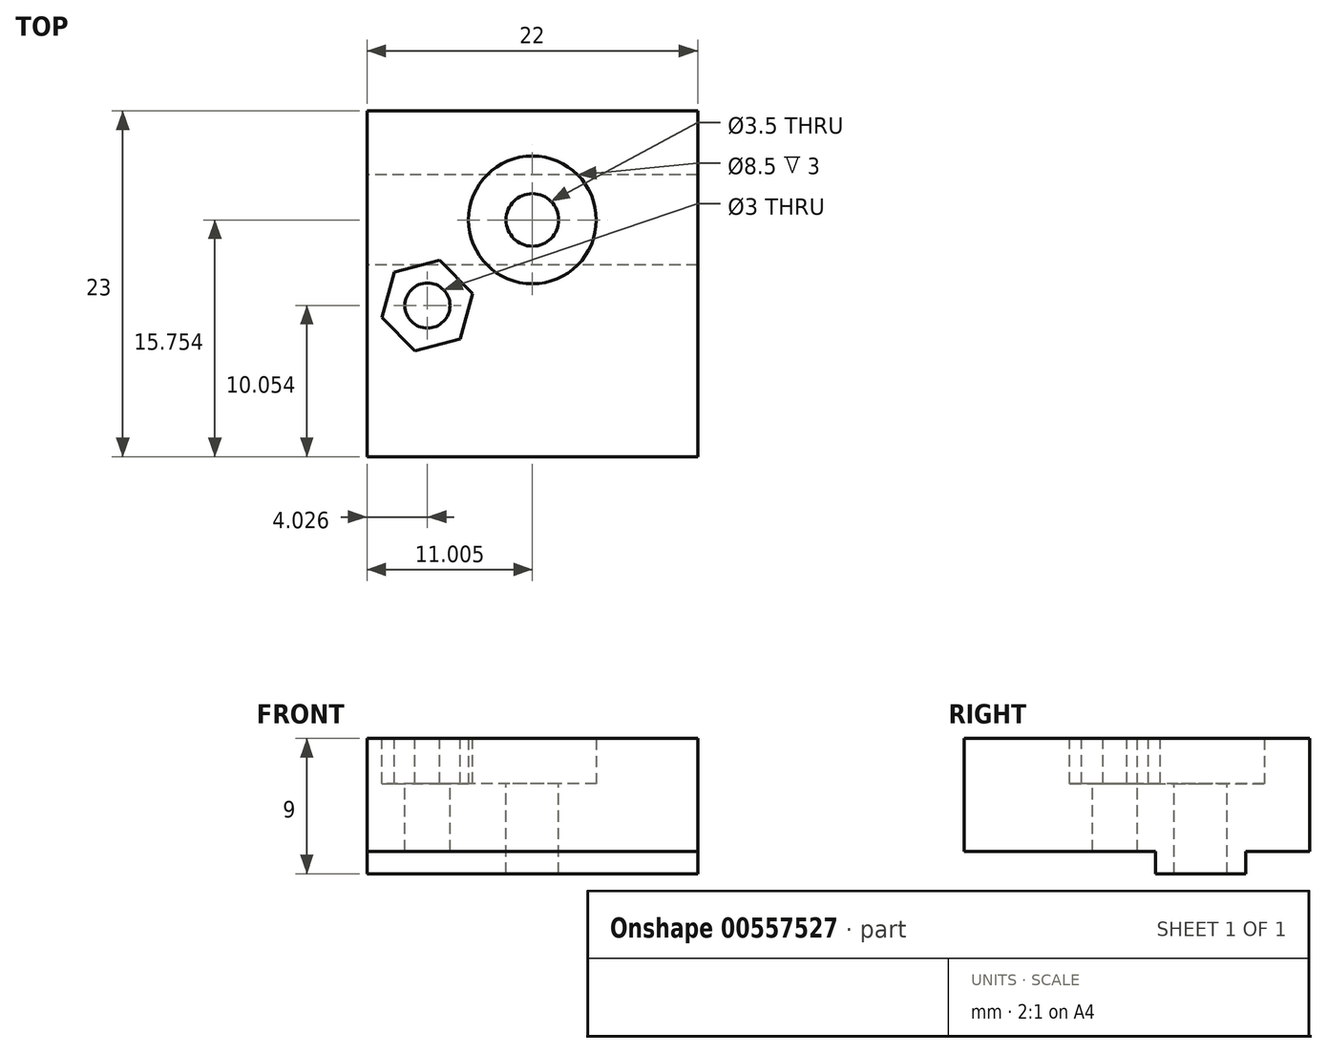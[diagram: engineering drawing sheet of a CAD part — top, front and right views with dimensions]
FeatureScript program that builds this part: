
annotation { "Feature Type Name" : "Feature", "Feature Type Description" : "" }
export const myFeature = defineFeature(function(context is Context, id is Id, definition is map)
    precondition{}
    {
        {
            var Q0;
            Q0=qCreatedBy(makeId("Top.planeOp"),FACE);
            var sketch = newSketch(context, id + "F0", { "sketchPlane" : qUnion([Q0])});
            skLineSegment(sketch, "E0.bottom", {"start": v(-9.07, 8.56) * mm, "end": v(12.93, 8.56) * mm});
            skLineSegment(sketch, "E0.top", {"start": v(-9.07, -14.44) * mm, "end": v(12.93, -14.44) * mm});
            skLineSegment(sketch, "E0.left", {"start": v(-9.07, 8.56) * mm, "end": v(-9.07, -14.44) * mm});
            skLineSegment(sketch, "E0.right", {"start": v(12.93, 8.56) * mm, "end": v(12.93, -14.44) * mm});
            skSolve(sketch);
        }
        {
            var Q0;
            Q0=makeQuery(id+"F0.imprint","IMPRINT",FACE,{"disambiguationData":[TD([[makeQuery(id+"F0.imprint","IMPRINT",EDGE,{"derivedFrom":sQuery(id+"F0.wireOp",EDGE,"E0.bottom")}),-1.0]])]});
            extrude(context, id + "F1", {"entities" : qUnion([Q0]), "depth" : 4.5 * mm, "offsetDistance" : 25 * mm});
        }
        {
            var Q0;
            Q0=makeQuery(id+"F1.opExtrude","CAP_FACE",FACE,{"disambiguationData":[OSD([sQuery(id+"F0.wireOp",EDGE,"E0.bottom"),sQuery(id+"F0.wireOp",EDGE,"E0.top"),sQuery(id+"F0.wireOp",EDGE,"E0.left"),sQuery(id+"F0.wireOp",EDGE,"E0.right")])],"isStart":false});
            var sketch = newSketch(context, id + "F2", { "sketchPlane" : qUnion([Q0])});
            skCircle(sketch, "E1", {"center": v(1.93, 1.31) * mm, "radius": 4.25 * mm});
            skPoint(sketch, "E1.centerSnap0", {"position": v(1.93, 8.56) * mm});
            skCircle(sketch, "E2", {"center": v(1.93, 1.31) * mm, "radius": 1.75 * mm});
            skPoint(sketch, "E3", {"position": v(12.93, -1.44) * mm});
            skPoint(sketch, "E4", {"position": v(-9.07, -10.44) * mm});
            skCircle(sketch, "E5.cCircle", {"center": v(-5.04, -4.39) * mm, "radius": 2.7 * mm, "construction": true});
            skLineSegment(sketch, "E5.0", {"start": v(-8.06, -5.17) * mm, "end": v(-7.24, -2.17) * mm});
            skLineSegment(sketch, "E5.1", {"start": v(-7.24, -2.17) * mm, "end": v(-4.22, -1.38) * mm});
            skLineSegment(sketch, "E5.2", {"start": v(-4.22, -1.38) * mm, "end": v(-2.03, -3.6) * mm});
            skLineSegment(sketch, "E5.3", {"start": v(-2.03, -3.6) * mm, "end": v(-2.85, -6.6) * mm});
            skLineSegment(sketch, "E5.4", {"start": v(-2.85, -6.6) * mm, "end": v(-5.87, -7.4) * mm});
            skLineSegment(sketch, "E5.5", {"start": v(-5.87, -7.4) * mm, "end": v(-8.06, -5.17) * mm});
            skPoint(sketch, "E5.0.midPoint", {"position": v(-7.65, -3.67) * mm});
            skCircle(sketch, "E6", {"center": v(-5.04, -4.39) * mm, "radius": 1.5 * mm});
            skSolve(sketch);
        }
        {
            var Q0;
            Q0=makeQuery(id+"F2.imprint","IMPRINT",FACE,{"disambiguationData":[TD([[makeQuery(id+"F2.imprint","IMPRINT",EDGE,{"derivedFrom":sQuery(id+"F2.wireOp",EDGE,"E2")}),1.0]])]});
            extrude(context, id + "F3", {"entities" : qUnion([Q0]), "operationType" : NewBodyOperationType.REMOVE, "endBound" : BoundingType.THROUGH_ALL, "oppositeDirection" : true, "depth" : 25 * mm, "offsetDistance" : 25 * mm});
        }
        {
            var Q0;
            Q0=makeQuery(id+"F1.opExtrude","CAP_FACE",FACE,{"disambiguationData":[OSD([sQuery(id+"F0.wireOp",EDGE,"E0.bottom"),sQuery(id+"F0.wireOp",EDGE,"E0.top"),sQuery(id+"F0.wireOp",EDGE,"E0.left"),sQuery(id+"F0.wireOp",EDGE,"E0.right")])],"isStart":true});
            var sketch = newSketch(context, id + "F4", { "sketchPlane" : qUnion([Q0])});
            skLineSegment(sketch, "E7.bottom", {"start": v(12.93, -4.31) * mm, "end": v(-9.07, -4.31) * mm});
            skLineSegment(sketch, "E7.top", {"start": v(12.93, 1.69) * mm, "end": v(-9.07, 1.69) * mm});
            skLineSegment(sketch, "E7.left", {"start": v(12.93, -4.31) * mm, "end": v(12.93, 1.69) * mm});
            skLineSegment(sketch, "E7.right", {"start": v(-9.07, -4.31) * mm, "end": v(-9.07, 1.69) * mm});
            skPoint(sketch, "E7.middle", {"position": v(1.93, -1.31) * mm});
            skSolve(sketch);
        }
        {
            var Q0;
            Q0=makeQuery(id+"F4.imprint","IMPRINT",FACE,{"disambiguationData":[TD([[makeQuery(id+"F4.imprint","IMPRINT",EDGE,{"derivedFrom":sQuery(id+"F4.wireOp",EDGE,"E7.bottom")}),-1.0]])]});
            extrude(context, id + "F5", {"entities" : qUnion([Q0]), "operationType" : NewBodyOperationType.ADD, "depth" : 1.5 * mm, "offsetDistance" : 25 * mm});
        }
        {
            var Q0;
            Q0=makeQuery(id+"F2.imprint","IMPRINT",FACE,{"disambiguationData":[TD([[makeQuery(id+"F2.imprint","IMPRINT",EDGE,{"derivedFrom":sQuery(id+"F2.wireOp",EDGE,"E1")}),-1.0]])]});
            var Q1;
            Q1=makeQuery(id+"F2.imprint","IMPRINT",FACE,{"disambiguationData":[TD([[makeQuery(id+"F2.imprint","IMPRINT",EDGE,{"derivedFrom":sQuery(id+"F2.wireOp",EDGE,"E5.0")}),-1.0]])]});
            var Q2;
            Q2=makeQuery(id+"F2.imprint","IMPRINT",FACE,{"disambiguationData":[TD([[makeQuery(id+"F2.imprint","IMPRINT",EDGE,{"derivedFrom":sQuery(id+"F2.wireOp",EDGE,"E6")}),1.0]])]});
            extrude(context, id + "F6", {"entities" : qUnion([Q0, Q1, Q2]), "operationType" : NewBodyOperationType.ADD, "depth" : 3 * mm, "offsetDistance" : 25 * mm});
        }
        {
            var Q0;
            Q0=makeQuery(id+"F6.opExtrude","CAP_FACE",FACE,{"disambiguationData":[OSD([sQuery(id+"F0.wireOp",EDGE,"E0.bottom"),sQuery(id+"F0.wireOp",EDGE,"E0.top"),sQuery(id+"F0.wireOp",EDGE,"E0.left"),sQuery(id+"F0.wireOp",EDGE,"E0.right"),sQuery(id+"F2.wireOp",EDGE,"E1")])],"isStart":false});
            var sketch = newSketch(context, id + "F7", { "sketchPlane" : qUnion([Q0])});
            skLineSegment(sketch, "E8.0", {"start": v(-4.22, -1.38) * mm, "end": v(-2.03, -3.6) * mm});
            skLineSegment(sketch, "E9.0", {"start": v(-7.24, -2.17) * mm, "end": v(-4.22, -1.38) * mm});
            skLineSegment(sketch, "E10.0", {"start": v(-8.06, -5.17) * mm, "end": v(-7.24, -2.17) * mm});
            skLineSegment(sketch, "E11.0", {"start": v(-5.87, -7.4) * mm, "end": v(-8.06, -5.17) * mm});
            skLineSegment(sketch, "E12.0", {"start": v(-2.85, -6.6) * mm, "end": v(-5.87, -7.4) * mm});
            skLineSegment(sketch, "E13.0", {"start": v(-2.03, -3.6) * mm, "end": v(-2.85, -6.6) * mm});
            skCircle(sketch, "E14.0", {"center": v(-5.04, -4.39) * mm, "radius": 1.5 * mm});
            skSolve(sketch);
        }
        {
            var Q0;
            Q0=makeQuery(id+"F7.imprint","IMPRINT",FACE,{"disambiguationData":[TD([[makeQuery(id+"F7.imprint","IMPRINT",EDGE,{"derivedFrom":sQuery(id+"F7.wireOp",EDGE,"E8.0")}),-1.0]])]});
            extrude(context, id + "F8", {"entities" : qUnion([Q0]), "operationType" : NewBodyOperationType.REMOVE, "oppositeDirection" : true, "depth" : 3 * mm, "offsetDistance" : 25 * mm});
        }
        {
            var Q0;
            Q0=makeQuery(id+"F8.boolean.opBoolean","SPLIT",FACE,{"disambiguationData":[TD([makeQuery(id+"F8.opExtrude","SWEPT_FACE",FACE,{"disambiguationData":[OSD([sQuery(id+"F7.wireOp",EDGE,"E14.0")])]})])],"derivedFrom":makeQuery(id+"F6.opExtrude","CAP_FACE",FACE,{"disambiguationData":[OSD([sQuery(id+"F0.wireOp",EDGE,"E0.bottom"),sQuery(id+"F0.wireOp",EDGE,"E0.top"),sQuery(id+"F0.wireOp",EDGE,"E0.left"),sQuery(id+"F0.wireOp",EDGE,"E0.right"),sQuery(id+"F2.wireOp",EDGE,"E1")])],"isStart":false})});
            extrude(context, id + "F9", {"entities" : qUnion([Q0]), "operationType" : NewBodyOperationType.REMOVE, "endBound" : BoundingType.THROUGH_ALL, "oppositeDirection" : true, "depth" : 25 * mm, "offsetDistance" : 25 * mm});
        }
    });
